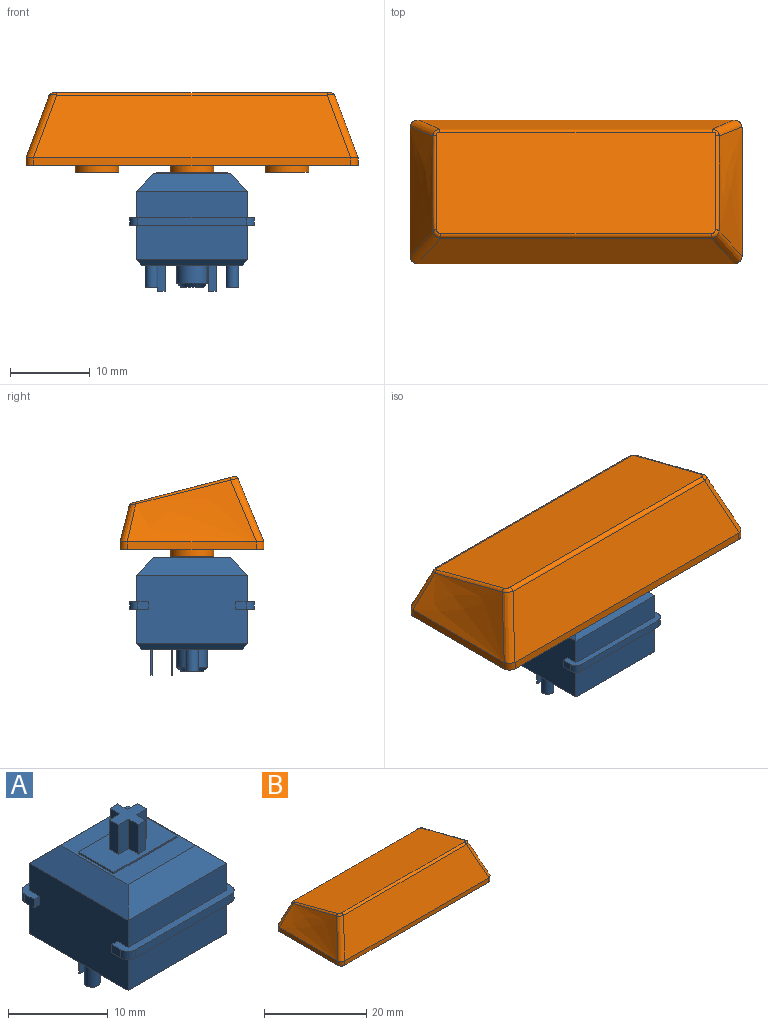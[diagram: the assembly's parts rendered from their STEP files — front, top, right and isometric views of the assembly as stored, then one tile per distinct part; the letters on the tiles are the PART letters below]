
ASSEMBLY  parts=2 mates=1
PART A: 69 faces, bbox 15.6x15.6x18.6 mm
  f0: plane 15.6x2.3mm, normal (0,0,-1), area 14.4mm2, adj f2,f3,f28,f30,f35,f60,f62,f63
  f1: plane 15.6x2.3mm, normal (0,0,-1), area 14.4mm2, adj f28,f30,f33,f34,f36,f59,f61,f64
  f2: plane 1.3x1mm, normal (1,0,0), area 1.3mm2, adj f0,f32,f62,f66
  f3: plane 1.3x1mm, normal (-1,0,0), area 1.3mm2, adj f0,f32,f63,f68
  f4: plane 15.6x2.3mm, normal (0,0,1), area 14.4mm2, adj f28,f30,f31,f33,f34,f36,f61,f64
  f5: plane 14x2.2mm, normal (-0.71,0,0.71), area 36.7mm2, adj f6,f7,f26,f30
  f6: plane 14x2.2mm, normal (0,-0.71,0.71), area 36.7mm2, adj f5,f7,f27,f31
  f7: plane 9.6x9.6mm, normal (0,0,1), area 47.2mm2, adj f5,f6,f8,f9,f10,f11,f26,f27
  f8: plane 5x0.2mm, normal (1,0,0), area 1mm2, adj f7,f9,f11,f12
  f9: plane 9x0.2mm, normal (0,1,0), area 1.8mm2, adj f7,f8,f10,f12
  f10: plane 5x0.2mm, normal (-1,0,0), area 1mm2, adj f7,f9,f11,f12
  f11: plane 9x0.2mm, normal (0,-1,0), area 1.8mm2, adj f7,f8,f10,f12
  f12: plane 9x5mm, normal (0,0,1), area 36.9mm2, adj f8,f9,f10,f11,f13,f14,f15,f16
  f13: plane 3.6x1.35mm, normal (1,0,0), area 4.9mm2, adj f12,f14,f24,f25
  f14: plane 3.6x1.08mm, normal (0,1,0), area 3.9mm2, adj f12,f13,f15,f25
  f15: plane 3.6x1.35mm, normal (-1,0,0), area 4.9mm2, adj f12,f14,f16,f25
  f16: plane 3.6x1.46mm, normal (0,1,0), area 5.3mm2, adj f12,f15,f17,f25
  f17: plane 3.6x1.3mm, normal (-1,0,0), area 4.7mm2, adj f12,f16,f18,f25
  f18: plane 3.6x1.46mm, normal (0,-1,0), area 5.3mm2, adj f12,f17,f19,f25
  f19: plane 3.6x1.35mm, normal (-1,0,0), area 4.9mm2, adj f12,f18,f20,f25
  f20: plane 3.6x1.08mm, normal (0,-1,0), area 3.9mm2, adj f12,f19,f21,f25
  f21: plane 3.6x1.35mm, normal (1,0,0), area 4.9mm2, adj f12,f20,f22,f25
  f22: plane 3.6x1.46mm, normal (0,-1,0), area 5.3mm2, adj f12,f21,f23,f25
  f23: plane 3.6x1.3mm, normal (1,0,0), area 4.7mm2, adj f12,f22,f24,f25
  f24: plane 3.6x1.46mm, normal (0,1,0), area 5.3mm2, adj f12,f13,f23,f25
  f25: plane 4x4mm, normal (0,0,1), area 8.1mm2, adj f13,f14,f15,f16,f17,f18,f19,f20
  f26: plane 14x2.2mm, normal (0,0.71,0.71), area 36.7mm2, adj f5,f7,f27,f29
  f27: plane 14x2.2mm, normal (0.71,0,0.71), area 36.7mm2, adj f6,f7,f26,f28
  f28: plane 14x8.6mm, normal (1,0,0), area 117.4mm2, adj f0,f1,f4,f27,f29,f31,f32,f55
  f29: plane 14x3.3mm, normal (0,1,0), area 46.2mm2, adj f26,f28,f30,f32
  f30: plane 14x8.6mm, normal (-1,0,0), area 117.4mm2, adj f0,f1,f4,f5,f29,f31,f32,f57
  f31: plane 14x3.3mm, normal (0,-1,0), area 46.2mm2, adj f4,f6,f28,f30
  f32: plane 15.6x2.3mm, normal (0,0,1), area 14.4mm2, adj f2,f3,f28,f29,f30,f35,f62,f63
  f33: plane 13.6x1mm, normal (0,-1,0), area 13.6mm2, adj f1,f4,f61,f64
  f34: plane 1.3x1mm, normal (1,0,0), area 1.3mm2, adj f1,f4,f61,f65
  f35: plane 13.6x1mm, normal (0,1,0), area 13.6mm2, adj f0,f32,f62,f63
  f36: plane 1.3x1mm, normal (-1,0,0), area 1.3mm2, adj f1,f4,f64,f67
  f37: plane 2.85x2.85mm, normal (0,0,-1), area 6.4mm2, adj f38
  f38: cone r=1.43mm half-angle=45deg, axis (0,0,1), area 7.4mm2, adj f37,f43
  f39: plane 1x0.2mm, normal (0,0,-1), area 0.2mm2, adj f44,f45,f46,f47
  f40: plane 1x0.2mm, normal (0,0,-1), area 0.2mm2, adj f48,f49,f50,f51
  f41: plane 1.6x1.6mm, normal (0,0,-1), area 2mm2, adj f52
  f42: plane 1.6x1.6mm, normal (0,0,-1), area 2mm2, adj f53
  f43: cylinder r=1.93mm len=3.85mm, axis (0,0,1), area 27.8mm2, adj f38,f54
  f44: plane 3.3x0.2mm, normal (-1,0,0), area 0.7mm2, adj f39,f45,f47,f54
  f45: plane 3.3x1mm, normal (0,1,0), area 3.3mm2, adj f39,f44,f46,f54
  f46: plane 3.3x0.2mm, normal (1,0,0), area 0.7mm2, adj f39,f45,f47,f54
  f47: plane 3.3x1mm, normal (0,-1,0), area 3.3mm2, adj f39,f44,f46,f54
  f48: plane 3.3x0.2mm, normal (-1,0,0), area 0.7mm2, adj f40,f49,f51,f54
  f49: plane 3.3x1mm, normal (0,1,0), area 3.3mm2, adj f40,f48,f50,f54
  f50: plane 3.3x0.2mm, normal (1,0,0), area 0.7mm2, adj f40,f49,f51,f54
  f51: plane 3.3x1mm, normal (0,-1,0), area 3.3mm2, adj f40,f48,f50,f54
  f52: cylinder r=0.8mm len=2.8mm, axis (0,0,1), area 14.1mm2, adj f41,f54
  f53: cylinder r=0.8mm len=2.8mm, axis (0,0,1), area 14.1mm2, adj f42,f54
  f54: plane 12.6x12.6mm, normal (0,0,-1), area 142.7mm2, adj f43,f44,f45,f46,f47,f48,f49,f50
  f55: plane 14x0.7mm, normal (0.71,0,-0.71), area 13.2mm2, adj f28,f54,f56,f58
  f56: plane 14x0.7mm, normal (0,0.71,-0.71), area 13.2mm2, adj f54,f55,f57,f60
  f57: plane 14x0.7mm, normal (-0.71,0,-0.71), area 13.2mm2, adj f30,f54,f56,f58
  f58: plane 14x0.7mm, normal (0,-0.71,-0.71), area 13.2mm2, adj f54,f55,f57,f59
  f59: plane 14x4.3mm, normal (0,-1,0), area 60.2mm2, adj f1,f28,f30,f58
  f60: plane 14x4.3mm, normal (0,1,0), area 60.2mm2, adj f0,f28,f30,f56
  f61: cylinder r=1mm len=1mm, axis (0,0,-1), area 1.6mm2, adj f1,f4,f33,f34
  f62: cylinder r=1mm len=1mm, axis (0,0,1), area 1.6mm2, adj f0,f2,f32,f35
  f63: cylinder r=1mm len=1mm, axis (0,0,-1), area 1.6mm2, adj f0,f3,f32,f35
  f64: cylinder r=1mm len=1mm, axis (0,0,1), area 1.6mm2, adj f1,f4,f33,f36
  f65: plane 1x0.8mm, normal (0,1,0), area 0.8mm2, adj f1,f4,f28,f34
  f66: plane 1x0.8mm, normal (0,-1,0), area 0.8mm2, adj f0,f2,f28,f32
  f67: plane 1x0.8mm, normal (0,1,0), area 0.8mm2, adj f1,f4,f30,f36
  f68: plane 1x0.8mm, normal (0,-1,0), area 0.8mm2, adj f0,f3,f30,f32
PART B: 80 faces, bbox 46x22.7x14.6 mm
  f0: plane 41.75x18.1mm, normal (0,0,-1), area 114.8mm2, adj f1,f2,f3,f4,f10,f12,f14,f16
  f1: plane 39.75x1mm, normal (0,-1,0), area 39.8mm2, adj f0,f8,f10,f12
  f2: plane 16.1x1mm, normal (1,0,0), area 16.1mm2, adj f0,f9,f10,f16
  f3: plane 39.75x1mm, normal (0,1,0), area 39.7mm2, adj f0,f6,f14,f15,f16,f17
  f4: plane 16.1x1mm, normal (-1,0,0), area 16.1mm2, adj f0,f7,f12,f14
  f5: plane 35.21x12.77mm, normal (0,0.25,0.97), area 462.9mm2, adj f18,f19,f20,f21,f22,f23,f24,f25
  f6: plane 39.71x4.53mm, normal (0,0.97,0.25), area 172.9mm2, adj f3,f15,f17,f20
  f7: bspline ~18.1x8.31mm, area 98.6mm2, adj f4,f12,f13,f14,f15,f19
  f8: plane 39.9x7.9mm, normal (0,-0.93,0.38), area 315.5mm2, adj f1,f10,f11,f12,f13,f23
  f9: bspline ~18.1x8.31mm, area 98.6mm2, adj f2,f10,f11,f16,f17,f24
  f10: cylinder r=1mm len=1.07mm, axis (0,0,1), area 1.6mm2, adj f0,f1,f2,f8,f9,f11
  f11: bspline ~11.3x5.51mm, area 13.2mm2, adj f8,f9,f10,f25
  f12: cylinder r=1mm len=1.07mm, axis (0,0,-1), area 1.6mm2, adj f0,f1,f4,f7,f8,f13
  f13: bspline ~11.44x5.57mm, area 13.2mm2, adj f7,f8,f12,f21
  f14: cylinder r=1mm len=1.01mm, axis (0,0,1), area 1.6mm2, adj f0,f3,f4,f7,f15
  f15: bspline ~7.23x4.95mm, area 7.7mm2, adj f3,f6,f7,f14,f18
  f16: cylinder r=1mm len=1.01mm, axis (0,0,-1), area 1.6mm2, adj f0,f2,f3,f9,f17
  f17: bspline ~7.14x4.9mm, area 7.7mm2, adj f3,f6,f9,f16,f22
  f18: bspline ~1.16x0.9mm, area 0.5mm2, adj f5,f15,f19,f20
  f19: bspline ~18.2x4.87mm, area 7mm2, adj f5,f7,f18,f21
  f20: cylinder r=0.5mm len=34.33mm, axis (-1,0,0), area 18.3mm2, adj f5,f6,f18,f22
  f21: bspline ~1.24x1.04mm, area 0.8mm2, adj f5,f13,f19,f23
  f22: bspline ~1.09x0.94mm, area 0.5mm2, adj f5,f17,f20,f24
  f23: cylinder r=0.5mm len=34.03mm, axis (-1,0,0), area 24.4mm2, adj f5,f8,f21,f25
  f24: bspline ~15.84x4.3mm, area 7mm2, adj f5,f9,f22,f25
  f25: bspline ~1.22x1.1mm, area 0.8mm2, adj f5,f11,f23,f24
  f26: plane 39.75x0.81mm, normal (0,1,0), area 31.9mm2, adj f0,f27,f29,f33
  f27: plane 16.18x0.9mm, normal (-1,0,0), area 12.4mm2, adj f0,f26,f28,f34
  f28: plane 39.75x0.87mm, normal (0,-1,0), area 34.7mm2, adj f0,f27,f29,f31,f32,f34
  f29: plane 16.18x0.9mm, normal (1,0,0), area 12.4mm2, adj f0,f26,f28,f32
  f30: plane 37.52x14.91mm, normal (0,-0.25,-0.97), area 355.8mm2, adj f31,f32,f33,f34,f46,f61,f76
  f31: plane 39.58x4.13mm, normal (0,-0.97,-0.25), area 157.7mm2, adj f28,f30,f32,f34
  f32: offset ~20.1x10.31mm, area 90.9mm2, adj f28,f29,f30,f31,f33
  f33: plane 39.8x7.36mm, normal (0,0.93,-0.38), area 292.8mm2, adj f26,f30,f32,f34
  f34: offset ~20.1x10.31mm, area 90.8mm2, adj f27,f28,f30,f31,f33
  f35: plane 7.77x1.5mm, normal (0,1,0), area 11.7mm2, adj f36,f44,f45,f49
  f36: plane 7.77x1.3mm, normal (1,0,0), area 9.9mm2, adj f35,f37,f45,f49
  f37: plane 7.44x1.5mm, normal (0,-1,0), area 11.2mm2, adj f36,f38,f45,f49
  f38: plane 7.44x1.35mm, normal (1,0,0), area 9.8mm2, adj f37,f39,f45,f49
  f39: plane 7.09x1mm, normal (0,-1,0), area 7.1mm2, adj f38,f40,f45,f49
  f40: plane 7.44x1.35mm, normal (-1,0,0), area 9.8mm2, adj f39,f41,f45,f49
  f41: plane 7.44x1.5mm, normal (0,-1,0), area 11.2mm2, adj f40,f42,f45,f49
  f42: plane 7.77x1.3mm, normal (-1,0,0), area 9.9mm2, adj f41,f43,f45,f49
  f43: plane 7.77x1.5mm, normal (0,1,0), area 11.7mm2, adj f42,f45,f47,f49
  f44: plane 8.12x1.35mm, normal (1,0,0), area 10.7mm2, adj f35,f45,f48,f49
  f45: plane 5.5x5.5mm, normal (0,0,-1), area 15.9mm2, adj f35,f36,f37,f38,f39,f40,f41,f42
  f46: cylinder r=2.75mm len=6.89mm, axis (0,0,-1), area 119.1mm2, adj f30,f45
  f47: plane 8.12x1.35mm, normal (-1,0,0), area 10.7mm2, adj f43,f45,f48,f49
  f48: plane 8.12x1mm, normal (0,1,0), area 8.1mm2, adj f44,f45,f47,f49
  f49: plane 4x4mm, normal (0,-0.25,-0.97), area 8.2mm2, adj f35,f36,f37,f38,f39,f40,f41,f42
  f50: plane 7.77x1.3mm, normal (-1,0,0), area 9.9mm2, adj f51,f59,f60,f64
  f51: plane 7.77x1.5mm, normal (0,1,0), area 11.7mm2, adj f50,f52,f60,f64
  f52: plane 8.12x1.35mm, normal (-1,0,0), area 10.7mm2, adj f51,f53,f60,f64
  f53: plane 8.12x1mm, normal (0,1,0), area 8.1mm2, adj f52,f54,f60,f64
  f54: plane 8.12x1.35mm, normal (1,0,0), area 10.7mm2, adj f53,f55,f60,f64
  f55: plane 7.77x1.5mm, normal (0,1,0), area 11.7mm2, adj f54,f56,f60,f64
  f56: plane 7.77x1.3mm, normal (1,0,0), area 9.9mm2, adj f55,f57,f60,f64
  f57: plane 7.44x1.5mm, normal (0,-1,0), area 11.2mm2, adj f56,f58,f60,f64
  f58: plane 7.44x1.35mm, normal (1,0,0), area 9.8mm2, adj f57,f60,f62,f64
  f59: plane 7.44x1.5mm, normal (0,-1,0), area 11.2mm2, adj f50,f60,f63,f64
  f60: plane 5.5x5.5mm, normal (0,0,-1), area 15.9mm2, adj f50,f51,f52,f53,f54,f55,f56,f57
  f61: cylinder r=2.75mm len=6.89mm, axis (0,0,-1), area 119.1mm2, adj f30,f60
  f62: plane 7.09x1mm, normal (0,-1,0), area 7.1mm2, adj f58,f60,f63,f64
  f63: plane 7.44x1.35mm, normal (-1,0,0), area 9.8mm2, adj f59,f60,f62,f64
  f64: plane 4x4mm, normal (0,-0.25,-0.97), area 8.2mm2, adj f50,f51,f52,f53,f54,f55,f56,f57
  f65: plane 7.77x1.3mm, normal (-1,0,0), area 9.9mm2, adj f66,f74,f75,f79
  f66: plane 7.77x1.5mm, normal (0,1,0), area 11.7mm2, adj f65,f67,f75,f79
  f67: plane 8.12x1.35mm, normal (-1,0,0), area 10.7mm2, adj f66,f68,f75,f79
  f68: plane 8.12x1mm, normal (0,1,0), area 8.1mm2, adj f67,f69,f75,f79
  f69: plane 8.12x1.35mm, normal (1,0,0), area 10.7mm2, adj f68,f70,f75,f79
  f70: plane 7.77x1.5mm, normal (0,1,0), area 11.7mm2, adj f69,f71,f75,f79
  f71: plane 7.77x1.3mm, normal (1,0,0), area 9.9mm2, adj f70,f72,f75,f79
  f72: plane 7.44x1.5mm, normal (0,-1,0), area 11.2mm2, adj f71,f73,f75,f79
  f73: plane 7.44x1.35mm, normal (1,0,0), area 9.8mm2, adj f72,f75,f77,f79
  f74: plane 7.44x1.5mm, normal (0,-1,0), area 11.2mm2, adj f65,f75,f78,f79
  f75: plane 5.5x5.5mm, normal (0,0,-1), area 15.9mm2, adj f65,f66,f67,f68,f69,f70,f71,f72
  f76: cylinder r=2.75mm len=6.89mm, axis (0,0,-1), area 119.1mm2, adj f30,f75
  f77: plane 7.09x1mm, normal (0,-1,0), area 7.1mm2, adj f73,f75,f78,f79
  f78: plane 7.44x1.35mm, normal (-1,0,0), area 9.8mm2, adj f74,f75,f77,f79
  f79: plane 4x4mm, normal (0,-0.25,-0.97), area 8.2mm2, adj f65,f66,f67,f68,f69,f70,f71,f72
PLACE A at identity fixed
PLACE B t=(0,0,11.7)mm
MATE fastened B.f46 <-> A.f38  axis (0,0,-1) through (0,0,11.7)mm
